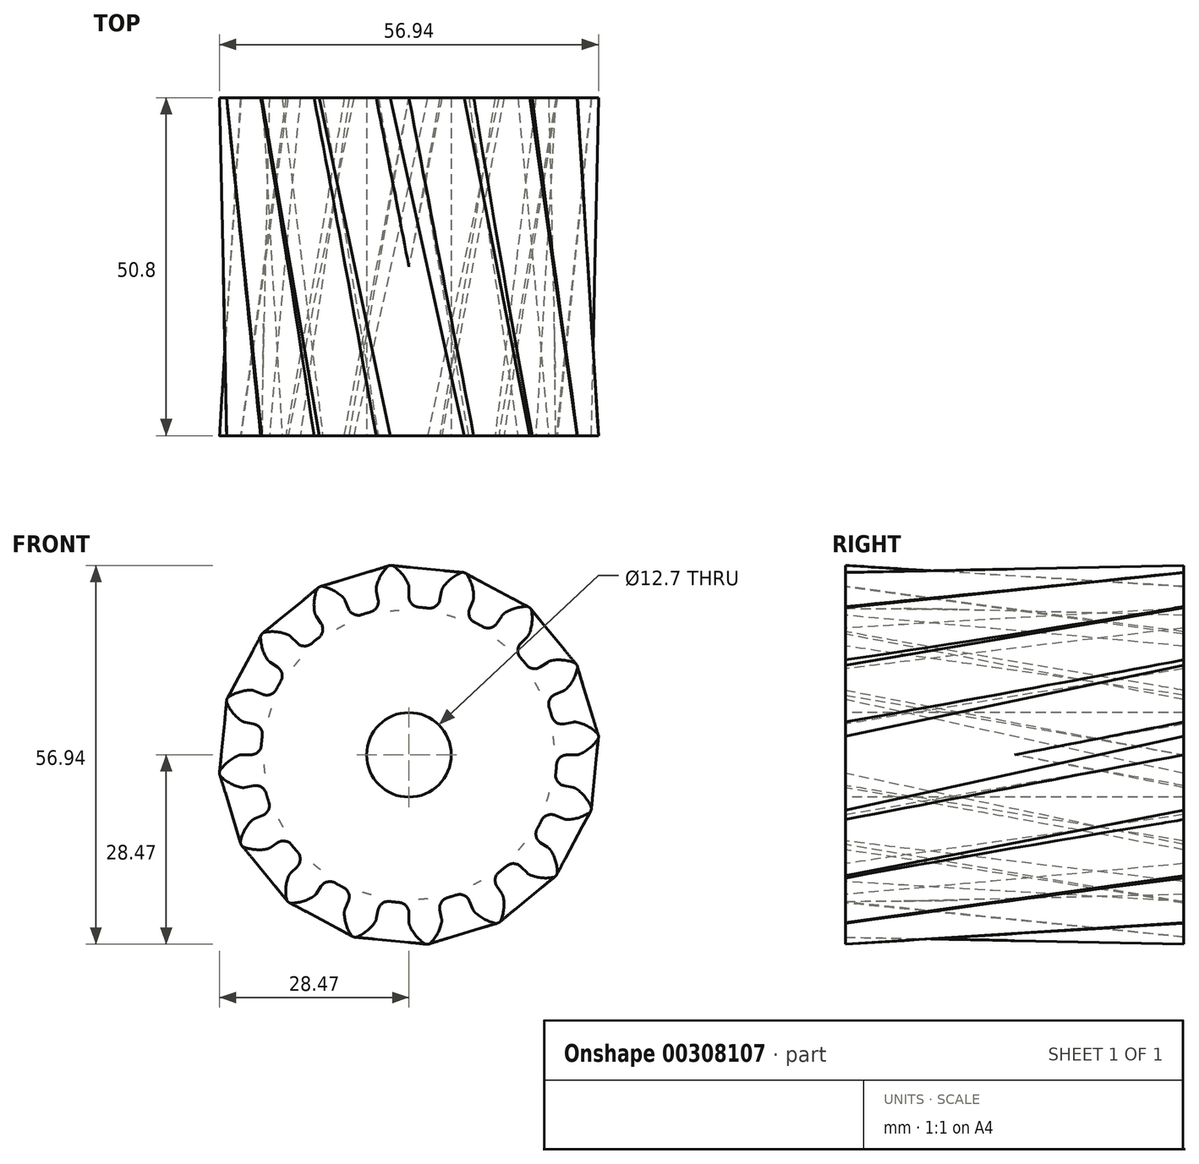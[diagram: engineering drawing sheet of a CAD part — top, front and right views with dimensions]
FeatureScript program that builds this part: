
annotation { "Feature Type Name" : "Feature", "Feature Type Description" : "" }
export const myFeature = defineFeature(function(context is Context, id is Id, definition is map)
    precondition{}
    {
        {
            var Q0;
            Q0=qCreatedBy(makeId("Front.planeOp"),FACE);
            var sketch = newSketch(context, id + "F0", { "sketchPlane" : qUnion([Q0])});
            skArc(sketch, "E0", {"start": v(-5.78, 21.46) * mm, "mid": v(-6.45, 21.27) * mm, "end": v(-7.11, 21.06) * mm});
            skArc(sketch, "E1.trimOffspring", {"start": v(-0.14, 25.74) * mm, "mid": v(-1.06, 27.21) * mm, "end": v(-2.36, 28.38) * mm});
            skLineSegment(sketch, "E2", {"start": v(-2.64, 28.47) * mm, "end": v(-2.8, 28.47) * mm});
            skLineSegment(sketch, "E3", {"start": v(0, 25.08) * mm, "end": v(0, 23.76) * mm});
            skLineSegment(sketch, "E4.MirrorCS", {"start": v(-2.96, 28.44) * mm, "end": v(-2.8, 28.47) * mm});
            skArc(sketch, "E5.MirrorCS", {"start": v(-4.89, 25.27) * mm, "mid": v(-4.27, 26.9) * mm, "end": v(-3.22, 28.3) * mm});
            skLineSegment(sketch, "E6.MirrorCS", {"start": v(-4.9, 24.6) * mm, "end": v(-4.64, 23.3) * mm});
            skPoint(sketch, "E7.orphan", {"position": v(-4.19, 21.03) * mm});
            skPoint(sketch, "E8.orphan", {"position": v(0, 21.44) * mm});
            skPoint(sketch, "E9.visualSharp", {"position": v(-3.1, 28.4) * mm});
            skArc(sketch, "E9.filletArc", {"start": v(-2.96, 28.44) * mm, "mid": v(-3.1, 28.38) * mm, "end": v(-3.22, 28.3) * mm});
            skPoint(sketch, "E10.visualSharp", {"position": v(-2.5, 28.47) * mm});
            skArc(sketch, "E10.filletArc", {"start": v(-2.36, 28.38) * mm, "mid": v(-2.5, 28.44) * mm, "end": v(-2.64, 28.47) * mm});
            skPoint(sketch, "E11.visualSharp", {"position": v(-4.96, 24.91) * mm});
            skArc(sketch, "E11.filletArc", {"start": v(-4.89, 25.27) * mm, "mid": v(-4.93, 24.94) * mm, "end": v(-4.9, 24.6) * mm});
            skPoint(sketch, "E12.visualSharp", {"position": v(0, 25.4) * mm});
            skArc(sketch, "E12.filletArc", {"start": v(0, 25.08) * mm, "mid": v(-0.03, 25.42) * mm, "end": v(-0.14, 25.74) * mm});
            skPoint(sketch, "E13.visualSharp", {"position": v(-4.34, 21.8) * mm});
            skArc(sketch, "E13.filletArc", {"start": v(-5.78, 21.46) * mm, "mid": v(-4.85, 22.15) * mm, "end": v(-4.64, 23.3) * mm});
            skPoint(sketch, "E14.visualSharp", {"position": v(0, 22.22) * mm});
            skArc(sketch, "E14.filletArc", {"start": v(0, 23.76) * mm, "mid": v(0.43, 22.67) * mm, "end": v(1.49, 22.18) * mm});
            skArc(sketch, "E15.1.0", {"start": v(-13.56, 17.61) * mm, "mid": v(-12.96, 18.61) * mm, "end": v(-13.2, 19.75) * mm});
            skLineSegment(sketch, "E15.1.1", {"start": v(-13.94, 20.85) * mm, "end": v(-13.2, 19.75) * mm});
            skArc(sketch, "E15.1.2", {"start": v(-14.19, 21.47) * mm, "mid": v(-14.1, 21.15) * mm, "end": v(-13.94, 20.85) * mm});
            skArc(sketch, "E15.1.3", {"start": v(-14.19, 21.47) * mm, "mid": v(-14.23, 23.22) * mm, "end": v(-13.8, 24.9) * mm});
            skArc(sketch, "E15.1.4", {"start": v(-13.62, 25.14) * mm, "mid": v(-13.73, 25.04) * mm, "end": v(-13.8, 24.9) * mm});
            skLineSegment(sketch, "E15.1.5", {"start": v(-13.62, 25.14) * mm, "end": v(-13.48, 25.23) * mm});
            skLineSegment(sketch, "E15.1.6", {"start": v(-13.34, 25.29) * mm, "end": v(-13.48, 25.23) * mm});
            skArc(sketch, "E15.1.7", {"start": v(-13.04, 25.32) * mm, "mid": v(-13.2, 25.32) * mm, "end": v(-13.34, 25.29) * mm});
            skArc(sketch, "E15.1.8", {"start": v(-9.97, 23.73) * mm, "mid": v(-11.4, 24.73) * mm, "end": v(-13.04, 25.32) * mm});
            skArc(sketch, "E15.1.9", {"start": v(-9.6, 23.18) * mm, "mid": v(-9.75, 23.47) * mm, "end": v(-9.97, 23.73) * mm});
            skLineSegment(sketch, "E15.1.10", {"start": v(-9.6, 23.18) * mm, "end": v(-9.09, 21.95) * mm});
            skArc(sketch, "E15.1.11", {"start": v(-9.09, 21.95) * mm, "mid": v(-8.28, 21.11) * mm, "end": v(-7.11, 21.06) * mm});
            skArc(sketch, "E15.2.0", {"start": v(-19.26, 11.08) * mm, "mid": v(-19.1, 12.24) * mm, "end": v(-19.76, 13.2) * mm});
            skLineSegment(sketch, "E15.2.1", {"start": v(-20.86, 13.93) * mm, "end": v(-19.76, 13.2) * mm});
            skArc(sketch, "E15.2.2", {"start": v(-21.32, 14.41) * mm, "mid": v(-21.12, 14.15) * mm, "end": v(-20.86, 13.93) * mm});
            skArc(sketch, "E15.2.3", {"start": v(-21.32, 14.41) * mm, "mid": v(-22.03, 16) * mm, "end": v(-22.29, 17.73) * mm});
            skArc(sketch, "E15.2.4", {"start": v(-22.2, 18.01) * mm, "mid": v(-22.26, 17.88) * mm, "end": v(-22.29, 17.73) * mm});
            skLineSegment(sketch, "E15.2.5", {"start": v(-22.2, 18.01) * mm, "end": v(-22.11, 18.15) * mm});
            skLineSegment(sketch, "E15.2.6", {"start": v(-22, 18.26) * mm, "end": v(-22.11, 18.15) * mm});
            skArc(sketch, "E15.2.7", {"start": v(-21.74, 18.4) * mm, "mid": v(-21.88, 18.35) * mm, "end": v(-22, 18.26) * mm});
            skArc(sketch, "E15.2.8", {"start": v(-18.3, 18.1) * mm, "mid": v(-20, 18.49) * mm, "end": v(-21.74, 18.4) * mm});
            skArc(sketch, "E15.2.9", {"start": v(-17.73, 17.74) * mm, "mid": v(-18, 17.95) * mm, "end": v(-18.3, 18.1) * mm});
            skLineSegment(sketch, "E15.2.10", {"start": v(-17.73, 17.74) * mm, "end": v(-16.8, 16.8) * mm});
            skArc(sketch, "E15.2.11", {"start": v(-16.8, 16.8) * mm, "mid": v(-15.73, 16.34) * mm, "end": v(-14.63, 16.73) * mm});
            skArc(sketch, "E15.3.0", {"start": v(-22.04, 2.87) * mm, "mid": v(-22.32, 4) * mm, "end": v(-23.3, 4.63) * mm});
            skLineSegment(sketch, "E15.3.1", {"start": v(-24.6, 4.89) * mm, "end": v(-23.3, 4.63) * mm});
            skArc(sketch, "E15.3.2", {"start": v(-25.22, 5.15) * mm, "mid": v(-24.92, 4.99) * mm, "end": v(-24.6, 4.89) * mm});
            skArc(sketch, "E15.3.3", {"start": v(-25.22, 5.15) * mm, "mid": v(-26.48, 6.35) * mm, "end": v(-27.37, 7.85) * mm});
            skArc(sketch, "E15.3.4", {"start": v(-27.4, 8.15) * mm, "mid": v(-27.41, 8) * mm, "end": v(-27.37, 7.85) * mm});
            skLineSegment(sketch, "E15.3.5", {"start": v(-27.4, 8.15) * mm, "end": v(-27.37, 8.3) * mm});
            skLineSegment(sketch, "E15.3.6", {"start": v(-27.31, 8.45) * mm, "end": v(-27.37, 8.3) * mm});
            skArc(sketch, "E15.3.7", {"start": v(-27.12, 8.68) * mm, "mid": v(-27.23, 8.58) * mm, "end": v(-27.31, 8.45) * mm});
            skArc(sketch, "E15.3.8", {"start": v(-23.83, 9.72) * mm, "mid": v(-25.55, 9.43) * mm, "end": v(-27.12, 8.68) * mm});
            skArc(sketch, "E15.3.9", {"start": v(-23.17, 9.6) * mm, "mid": v(-23.5, 9.7) * mm, "end": v(-23.83, 9.72) * mm});
            skLineSegment(sketch, "E15.3.10", {"start": v(-23.17, 9.6) * mm, "end": v(-21.95, 9.1) * mm});
            skArc(sketch, "E15.3.11", {"start": v(-21.95, 9.1) * mm, "mid": v(-20.78, 9.08) * mm, "end": v(-19.92, 9.86) * mm});
            skArc(sketch, "E15.4.0", {"start": v(-21.46, -5.78) * mm, "mid": v(-22.15, -4.85) * mm, "end": v(-23.3, -4.64) * mm});
            skLineSegment(sketch, "E15.4.1", {"start": v(-24.6, -4.9) * mm, "end": v(-23.3, -4.64) * mm});
            skArc(sketch, "E15.4.2", {"start": v(-25.27, -4.89) * mm, "mid": v(-24.94, -4.93) * mm, "end": v(-24.6, -4.9) * mm});
            skArc(sketch, "E15.4.3", {"start": v(-25.27, -4.89) * mm, "mid": v(-26.9, -4.27) * mm, "end": v(-28.3, -3.22) * mm});
            skArc(sketch, "E15.4.4", {"start": v(-28.44, -2.96) * mm, "mid": v(-28.38, -3.1) * mm, "end": v(-28.3, -3.22) * mm});
            skLineSegment(sketch, "E15.4.5", {"start": v(-28.44, -2.96) * mm, "end": v(-28.47, -2.8) * mm});
            skLineSegment(sketch, "E15.4.6", {"start": v(-28.47, -2.64) * mm, "end": v(-28.47, -2.8) * mm});
            skArc(sketch, "E15.4.7", {"start": v(-28.38, -2.36) * mm, "mid": v(-28.44, -2.5) * mm, "end": v(-28.47, -2.64) * mm});
            skArc(sketch, "E15.4.8", {"start": v(-25.74, -0.14) * mm, "mid": v(-27.21, -1.06) * mm, "end": v(-28.38, -2.36) * mm});
            skArc(sketch, "E15.4.9", {"start": v(-25.08, 0) * mm, "mid": v(-25.42, -0.03) * mm, "end": v(-25.74, -0.14) * mm});
            skLineSegment(sketch, "E15.4.10", {"start": v(-25.08, 0) * mm, "end": v(-23.76, 0) * mm});
            skArc(sketch, "E15.4.11", {"start": v(-23.76, 0) * mm, "mid": v(-22.67, 0.43) * mm, "end": v(-22.18, 1.49) * mm});
            skArc(sketch, "E15.5.0", {"start": v(-17.61, -13.56) * mm, "mid": v(-18.61, -12.96) * mm, "end": v(-19.75, -13.2) * mm});
            skLineSegment(sketch, "E15.5.1", {"start": v(-20.85, -13.94) * mm, "end": v(-19.75, -13.2) * mm});
            skArc(sketch, "E15.5.2", {"start": v(-21.47, -14.19) * mm, "mid": v(-21.15, -14.1) * mm, "end": v(-20.85, -13.94) * mm});
            skArc(sketch, "E15.5.3", {"start": v(-21.47, -14.19) * mm, "mid": v(-23.22, -14.23) * mm, "end": v(-24.9, -13.8) * mm});
            skArc(sketch, "E15.5.4", {"start": v(-25.14, -13.62) * mm, "mid": v(-25.04, -13.73) * mm, "end": v(-24.9, -13.8) * mm});
            skLineSegment(sketch, "E15.5.5", {"start": v(-25.14, -13.62) * mm, "end": v(-25.23, -13.48) * mm});
            skLineSegment(sketch, "E15.5.6", {"start": v(-25.29, -13.34) * mm, "end": v(-25.23, -13.48) * mm});
            skArc(sketch, "E15.5.7", {"start": v(-25.32, -13.04) * mm, "mid": v(-25.32, -13.2) * mm, "end": v(-25.29, -13.34) * mm});
            skArc(sketch, "E15.5.8", {"start": v(-23.73, -9.97) * mm, "mid": v(-24.73, -11.4) * mm, "end": v(-25.32, -13.04) * mm});
            skArc(sketch, "E15.5.9", {"start": v(-23.18, -9.6) * mm, "mid": v(-23.47, -9.75) * mm, "end": v(-23.73, -9.97) * mm});
            skLineSegment(sketch, "E15.5.10", {"start": v(-23.18, -9.6) * mm, "end": v(-21.95, -9.09) * mm});
            skArc(sketch, "E15.5.11", {"start": v(-21.95, -9.09) * mm, "mid": v(-21.11, -8.28) * mm, "end": v(-21.06, -7.11) * mm});
            skArc(sketch, "E15.6.0", {"start": v(-11.08, -19.26) * mm, "mid": v(-12.24, -19.1) * mm, "end": v(-13.2, -19.76) * mm});
            skLineSegment(sketch, "E15.6.1", {"start": v(-13.93, -20.86) * mm, "end": v(-13.2, -19.76) * mm});
            skArc(sketch, "E15.6.2", {"start": v(-14.41, -21.32) * mm, "mid": v(-14.15, -21.12) * mm, "end": v(-13.93, -20.86) * mm});
            skArc(sketch, "E15.6.3", {"start": v(-14.41, -21.32) * mm, "mid": v(-16, -22.03) * mm, "end": v(-17.73, -22.29) * mm});
            skArc(sketch, "E15.6.4", {"start": v(-18.01, -22.2) * mm, "mid": v(-17.88, -22.26) * mm, "end": v(-17.73, -22.29) * mm});
            skLineSegment(sketch, "E15.6.5", {"start": v(-18.01, -22.2) * mm, "end": v(-18.15, -22.11) * mm});
            skLineSegment(sketch, "E15.6.6", {"start": v(-18.26, -22) * mm, "end": v(-18.15, -22.11) * mm});
            skArc(sketch, "E15.6.7", {"start": v(-18.4, -21.74) * mm, "mid": v(-18.35, -21.88) * mm, "end": v(-18.26, -22) * mm});
            skArc(sketch, "E15.6.8", {"start": v(-18.1, -18.3) * mm, "mid": v(-18.49, -20) * mm, "end": v(-18.4, -21.74) * mm});
            skArc(sketch, "E15.6.9", {"start": v(-17.74, -17.73) * mm, "mid": v(-17.95, -18) * mm, "end": v(-18.1, -18.3) * mm});
            skLineSegment(sketch, "E15.6.10", {"start": v(-17.74, -17.73) * mm, "end": v(-16.8, -16.8) * mm});
            skArc(sketch, "E15.6.11", {"start": v(-16.8, -16.8) * mm, "mid": v(-16.34, -15.73) * mm, "end": v(-16.73, -14.63) * mm});
            skArc(sketch, "E15.7.0", {"start": v(-2.87, -22.04) * mm, "mid": v(-4, -22.32) * mm, "end": v(-4.63, -23.3) * mm});
            skLineSegment(sketch, "E15.7.1", {"start": v(-4.89, -24.6) * mm, "end": v(-4.63, -23.3) * mm});
            skArc(sketch, "E15.7.2", {"start": v(-5.15, -25.22) * mm, "mid": v(-4.99, -24.92) * mm, "end": v(-4.89, -24.6) * mm});
            skArc(sketch, "E15.7.3", {"start": v(-5.15, -25.22) * mm, "mid": v(-6.35, -26.48) * mm, "end": v(-7.85, -27.37) * mm});
            skArc(sketch, "E15.7.4", {"start": v(-8.15, -27.4) * mm, "mid": v(-8, -27.41) * mm, "end": v(-7.85, -27.37) * mm});
            skLineSegment(sketch, "E15.7.5", {"start": v(-8.15, -27.4) * mm, "end": v(-8.3, -27.37) * mm});
            skLineSegment(sketch, "E15.7.6", {"start": v(-8.45, -27.31) * mm, "end": v(-8.3, -27.37) * mm});
            skArc(sketch, "E15.7.7", {"start": v(-8.68, -27.12) * mm, "mid": v(-8.58, -27.23) * mm, "end": v(-8.45, -27.31) * mm});
            skArc(sketch, "E15.7.8", {"start": v(-9.72, -23.83) * mm, "mid": v(-9.43, -25.55) * mm, "end": v(-8.68, -27.12) * mm});
            skArc(sketch, "E15.7.9", {"start": v(-9.6, -23.17) * mm, "mid": v(-9.7, -23.5) * mm, "end": v(-9.72, -23.83) * mm});
            skLineSegment(sketch, "E15.7.10", {"start": v(-9.6, -23.17) * mm, "end": v(-9.1, -21.95) * mm});
            skArc(sketch, "E15.7.11", {"start": v(-9.1, -21.95) * mm, "mid": v(-9.08, -20.78) * mm, "end": v(-9.86, -19.92) * mm});
            skArc(sketch, "E15.8.0", {"start": v(5.78, -21.46) * mm, "mid": v(4.85, -22.15) * mm, "end": v(4.64, -23.3) * mm});
            skLineSegment(sketch, "E15.8.1", {"start": v(4.9, -24.6) * mm, "end": v(4.64, -23.3) * mm});
            skArc(sketch, "E15.8.2", {"start": v(4.89, -25.27) * mm, "mid": v(4.93, -24.94) * mm, "end": v(4.9, -24.6) * mm});
            skArc(sketch, "E15.8.3", {"start": v(4.89, -25.27) * mm, "mid": v(4.27, -26.9) * mm, "end": v(3.22, -28.3) * mm});
            skArc(sketch, "E15.8.4", {"start": v(2.96, -28.44) * mm, "mid": v(3.1, -28.38) * mm, "end": v(3.22, -28.3) * mm});
            skLineSegment(sketch, "E15.8.5", {"start": v(2.96, -28.44) * mm, "end": v(2.8, -28.47) * mm});
            skLineSegment(sketch, "E15.8.6", {"start": v(2.64, -28.47) * mm, "end": v(2.8, -28.47) * mm});
            skArc(sketch, "E15.8.7", {"start": v(2.36, -28.38) * mm, "mid": v(2.5, -28.44) * mm, "end": v(2.64, -28.47) * mm});
            skArc(sketch, "E15.8.8", {"start": v(0.14, -25.74) * mm, "mid": v(1.06, -27.21) * mm, "end": v(2.36, -28.38) * mm});
            skArc(sketch, "E15.8.9", {"start": v(0, -25.08) * mm, "mid": v(0.03, -25.42) * mm, "end": v(0.14, -25.74) * mm});
            skLineSegment(sketch, "E15.8.10", {"start": v(0, -25.08) * mm, "end": v(0, -23.76) * mm});
            skArc(sketch, "E15.8.11", {"start": v(0, -23.76) * mm, "mid": v(-0.43, -22.67) * mm, "end": v(-1.49, -22.18) * mm});
            skArc(sketch, "E15.9.0", {"start": v(13.56, -17.61) * mm, "mid": v(12.96, -18.61) * mm, "end": v(13.2, -19.75) * mm});
            skLineSegment(sketch, "E15.9.1", {"start": v(13.94, -20.85) * mm, "end": v(13.2, -19.75) * mm});
            skArc(sketch, "E15.9.2", {"start": v(14.19, -21.47) * mm, "mid": v(14.1, -21.15) * mm, "end": v(13.94, -20.85) * mm});
            skArc(sketch, "E15.9.3", {"start": v(14.19, -21.47) * mm, "mid": v(14.23, -23.22) * mm, "end": v(13.8, -24.9) * mm});
            skArc(sketch, "E15.9.4", {"start": v(13.62, -25.14) * mm, "mid": v(13.73, -25.04) * mm, "end": v(13.8, -24.9) * mm});
            skLineSegment(sketch, "E15.9.5", {"start": v(13.62, -25.14) * mm, "end": v(13.48, -25.23) * mm});
            skLineSegment(sketch, "E15.9.6", {"start": v(13.34, -25.29) * mm, "end": v(13.48, -25.23) * mm});
            skArc(sketch, "E15.9.7", {"start": v(13.04, -25.32) * mm, "mid": v(13.2, -25.32) * mm, "end": v(13.34, -25.29) * mm});
            skArc(sketch, "E15.9.8", {"start": v(9.97, -23.73) * mm, "mid": v(11.4, -24.73) * mm, "end": v(13.04, -25.32) * mm});
            skArc(sketch, "E15.9.9", {"start": v(9.6, -23.18) * mm, "mid": v(9.75, -23.47) * mm, "end": v(9.97, -23.73) * mm});
            skLineSegment(sketch, "E15.9.10", {"start": v(9.6, -23.18) * mm, "end": v(9.09, -21.95) * mm});
            skArc(sketch, "E15.9.11", {"start": v(9.09, -21.95) * mm, "mid": v(8.28, -21.11) * mm, "end": v(7.11, -21.06) * mm});
            skArc(sketch, "E15.10.0", {"start": v(19.26, -11.08) * mm, "mid": v(19.1, -12.24) * mm, "end": v(19.76, -13.2) * mm});
            skLineSegment(sketch, "E15.10.1", {"start": v(20.86, -13.93) * mm, "end": v(19.76, -13.2) * mm});
            skArc(sketch, "E15.10.2", {"start": v(21.32, -14.41) * mm, "mid": v(21.12, -14.15) * mm, "end": v(20.86, -13.93) * mm});
            skArc(sketch, "E15.10.3", {"start": v(21.32, -14.41) * mm, "mid": v(22.03, -16) * mm, "end": v(22.29, -17.73) * mm});
            skArc(sketch, "E15.10.4", {"start": v(22.2, -18.01) * mm, "mid": v(22.26, -17.88) * mm, "end": v(22.29, -17.73) * mm});
            skLineSegment(sketch, "E15.10.5", {"start": v(22.2, -18.01) * mm, "end": v(22.11, -18.15) * mm});
            skLineSegment(sketch, "E15.10.6", {"start": v(22, -18.26) * mm, "end": v(22.11, -18.15) * mm});
            skArc(sketch, "E15.10.7", {"start": v(21.74, -18.4) * mm, "mid": v(21.88, -18.35) * mm, "end": v(22, -18.26) * mm});
            skArc(sketch, "E15.10.8", {"start": v(18.3, -18.1) * mm, "mid": v(20, -18.49) * mm, "end": v(21.74, -18.4) * mm});
            skArc(sketch, "E15.10.9", {"start": v(17.73, -17.74) * mm, "mid": v(18, -17.95) * mm, "end": v(18.3, -18.1) * mm});
            skLineSegment(sketch, "E15.10.10", {"start": v(17.73, -17.74) * mm, "end": v(16.8, -16.8) * mm});
            skArc(sketch, "E15.10.11", {"start": v(16.8, -16.8) * mm, "mid": v(15.73, -16.34) * mm, "end": v(14.63, -16.73) * mm});
            skArc(sketch, "E15.11.0", {"start": v(22.04, -2.87) * mm, "mid": v(22.32, -4) * mm, "end": v(23.3, -4.63) * mm});
            skLineSegment(sketch, "E15.11.1", {"start": v(24.6, -4.89) * mm, "end": v(23.3, -4.63) * mm});
            skArc(sketch, "E15.11.2", {"start": v(25.22, -5.15) * mm, "mid": v(24.92, -4.99) * mm, "end": v(24.6, -4.89) * mm});
            skArc(sketch, "E15.11.3", {"start": v(25.22, -5.15) * mm, "mid": v(26.48, -6.35) * mm, "end": v(27.37, -7.85) * mm});
            skArc(sketch, "E15.11.4", {"start": v(27.4, -8.15) * mm, "mid": v(27.41, -8) * mm, "end": v(27.37, -7.85) * mm});
            skLineSegment(sketch, "E15.11.5", {"start": v(27.4, -8.15) * mm, "end": v(27.37, -8.3) * mm});
            skLineSegment(sketch, "E15.11.6", {"start": v(27.31, -8.45) * mm, "end": v(27.37, -8.3) * mm});
            skArc(sketch, "E15.11.7", {"start": v(27.12, -8.68) * mm, "mid": v(27.23, -8.58) * mm, "end": v(27.31, -8.45) * mm});
            skArc(sketch, "E15.11.8", {"start": v(23.83, -9.72) * mm, "mid": v(25.55, -9.43) * mm, "end": v(27.12, -8.68) * mm});
            skArc(sketch, "E15.11.9", {"start": v(23.17, -9.6) * mm, "mid": v(23.5, -9.7) * mm, "end": v(23.83, -9.72) * mm});
            skLineSegment(sketch, "E15.11.10", {"start": v(23.17, -9.6) * mm, "end": v(21.95, -9.1) * mm});
            skArc(sketch, "E15.11.11", {"start": v(21.95, -9.1) * mm, "mid": v(20.78, -9.08) * mm, "end": v(19.92, -9.86) * mm});
            skArc(sketch, "E15.12.0", {"start": v(21.46, 5.78) * mm, "mid": v(22.15, 4.85) * mm, "end": v(23.3, 4.64) * mm});
            skLineSegment(sketch, "E15.12.1", {"start": v(24.6, 4.9) * mm, "end": v(23.3, 4.64) * mm});
            skArc(sketch, "E15.12.2", {"start": v(25.27, 4.89) * mm, "mid": v(24.94, 4.93) * mm, "end": v(24.6, 4.9) * mm});
            skArc(sketch, "E15.12.3", {"start": v(25.27, 4.89) * mm, "mid": v(26.9, 4.27) * mm, "end": v(28.3, 3.22) * mm});
            skArc(sketch, "E15.12.4", {"start": v(28.44, 2.96) * mm, "mid": v(28.38, 3.1) * mm, "end": v(28.3, 3.22) * mm});
            skLineSegment(sketch, "E15.12.5", {"start": v(28.44, 2.96) * mm, "end": v(28.47, 2.8) * mm});
            skLineSegment(sketch, "E15.12.6", {"start": v(28.47, 2.64) * mm, "end": v(28.47, 2.8) * mm});
            skArc(sketch, "E15.12.7", {"start": v(28.38, 2.36) * mm, "mid": v(28.44, 2.5) * mm, "end": v(28.47, 2.64) * mm});
            skArc(sketch, "E15.12.8", {"start": v(25.74, 0.14) * mm, "mid": v(27.21, 1.06) * mm, "end": v(28.38, 2.36) * mm});
            skArc(sketch, "E15.12.9", {"start": v(25.08, 0) * mm, "mid": v(25.42, 0.03) * mm, "end": v(25.74, 0.14) * mm});
            skLineSegment(sketch, "E15.12.10", {"start": v(25.08, 0) * mm, "end": v(23.76, 0) * mm});
            skArc(sketch, "E15.12.11", {"start": v(23.76, 0) * mm, "mid": v(22.67, -0.43) * mm, "end": v(22.18, -1.49) * mm});
            skArc(sketch, "E15.13.0", {"start": v(17.61, 13.56) * mm, "mid": v(18.61, 12.96) * mm, "end": v(19.75, 13.2) * mm});
            skLineSegment(sketch, "E15.13.1", {"start": v(20.85, 13.94) * mm, "end": v(19.75, 13.2) * mm});
            skArc(sketch, "E15.13.2", {"start": v(21.47, 14.19) * mm, "mid": v(21.15, 14.1) * mm, "end": v(20.85, 13.94) * mm});
            skArc(sketch, "E15.13.3", {"start": v(21.47, 14.19) * mm, "mid": v(23.22, 14.23) * mm, "end": v(24.9, 13.8) * mm});
            skArc(sketch, "E15.13.4", {"start": v(25.14, 13.62) * mm, "mid": v(25.04, 13.73) * mm, "end": v(24.9, 13.8) * mm});
            skLineSegment(sketch, "E15.13.5", {"start": v(25.14, 13.62) * mm, "end": v(25.23, 13.48) * mm});
            skLineSegment(sketch, "E15.13.6", {"start": v(25.29, 13.34) * mm, "end": v(25.23, 13.48) * mm});
            skArc(sketch, "E15.13.7", {"start": v(25.32, 13.04) * mm, "mid": v(25.32, 13.2) * mm, "end": v(25.29, 13.34) * mm});
            skArc(sketch, "E15.13.8", {"start": v(23.73, 9.97) * mm, "mid": v(24.73, 11.4) * mm, "end": v(25.32, 13.04) * mm});
            skArc(sketch, "E15.13.9", {"start": v(23.18, 9.6) * mm, "mid": v(23.47, 9.75) * mm, "end": v(23.73, 9.97) * mm});
            skLineSegment(sketch, "E15.13.10", {"start": v(23.18, 9.6) * mm, "end": v(21.95, 9.09) * mm});
            skArc(sketch, "E15.13.11", {"start": v(21.95, 9.09) * mm, "mid": v(21.11, 8.28) * mm, "end": v(21.06, 7.11) * mm});
            skArc(sketch, "E15.14.0", {"start": v(11.08, 19.26) * mm, "mid": v(12.24, 19.1) * mm, "end": v(13.2, 19.76) * mm});
            skLineSegment(sketch, "E15.14.1", {"start": v(13.93, 20.86) * mm, "end": v(13.2, 19.76) * mm});
            skArc(sketch, "E15.14.2", {"start": v(14.41, 21.32) * mm, "mid": v(14.15, 21.12) * mm, "end": v(13.93, 20.86) * mm});
            skArc(sketch, "E15.14.3", {"start": v(14.41, 21.32) * mm, "mid": v(16, 22.03) * mm, "end": v(17.73, 22.29) * mm});
            skArc(sketch, "E15.14.4", {"start": v(18.01, 22.2) * mm, "mid": v(17.88, 22.26) * mm, "end": v(17.73, 22.29) * mm});
            skLineSegment(sketch, "E15.14.5", {"start": v(18.01, 22.2) * mm, "end": v(18.15, 22.11) * mm});
            skLineSegment(sketch, "E15.14.6", {"start": v(18.26, 22) * mm, "end": v(18.15, 22.11) * mm});
            skArc(sketch, "E15.14.7", {"start": v(18.4, 21.74) * mm, "mid": v(18.35, 21.88) * mm, "end": v(18.26, 22) * mm});
            skArc(sketch, "E15.14.8", {"start": v(18.1, 18.3) * mm, "mid": v(18.49, 20) * mm, "end": v(18.4, 21.74) * mm});
            skArc(sketch, "E15.14.9", {"start": v(17.74, 17.73) * mm, "mid": v(17.95, 18) * mm, "end": v(18.1, 18.3) * mm});
            skLineSegment(sketch, "E15.14.10", {"start": v(17.74, 17.73) * mm, "end": v(16.8, 16.8) * mm});
            skArc(sketch, "E15.14.11", {"start": v(16.8, 16.8) * mm, "mid": v(16.34, 15.73) * mm, "end": v(16.73, 14.63) * mm});
            skArc(sketch, "E15.15.0", {"start": v(2.87, 22.04) * mm, "mid": v(4, 22.32) * mm, "end": v(4.63, 23.3) * mm});
            skLineSegment(sketch, "E15.15.1", {"start": v(4.89, 24.6) * mm, "end": v(4.63, 23.3) * mm});
            skArc(sketch, "E15.15.2", {"start": v(5.15, 25.22) * mm, "mid": v(4.99, 24.92) * mm, "end": v(4.89, 24.6) * mm});
            skArc(sketch, "E15.15.3", {"start": v(5.15, 25.22) * mm, "mid": v(6.35, 26.48) * mm, "end": v(7.85, 27.37) * mm});
            skArc(sketch, "E15.15.4", {"start": v(8.15, 27.4) * mm, "mid": v(8, 27.41) * mm, "end": v(7.85, 27.37) * mm});
            skLineSegment(sketch, "E15.15.5", {"start": v(8.15, 27.4) * mm, "end": v(8.3, 27.37) * mm});
            skLineSegment(sketch, "E15.15.6", {"start": v(8.45, 27.31) * mm, "end": v(8.3, 27.37) * mm});
            skArc(sketch, "E15.15.7", {"start": v(8.68, 27.12) * mm, "mid": v(8.58, 27.23) * mm, "end": v(8.45, 27.31) * mm});
            skArc(sketch, "E15.15.8", {"start": v(9.72, 23.83) * mm, "mid": v(9.43, 25.55) * mm, "end": v(8.68, 27.12) * mm});
            skArc(sketch, "E15.15.9", {"start": v(9.6, 23.17) * mm, "mid": v(9.7, 23.5) * mm, "end": v(9.72, 23.83) * mm});
            skLineSegment(sketch, "E15.15.10", {"start": v(9.6, 23.17) * mm, "end": v(9.1, 21.95) * mm});
            skArc(sketch, "E15.15.11", {"start": v(9.1, 21.95) * mm, "mid": v(9.08, 20.78) * mm, "end": v(9.86, 19.92) * mm});
            skArc(sketch, "E16.trimOffspring", {"start": v(-17.61, -13.56) * mm, "mid": v(-17.18, -14.1) * mm, "end": v(-16.73, -14.63) * mm});
            skArc(sketch, "E17.trimOffspring", {"start": v(-21.46, -5.78) * mm, "mid": v(-21.27, -6.45) * mm, "end": v(-21.06, -7.11) * mm});
            skArc(sketch, "E18.trimOffspring", {"start": v(-22.04, 2.87) * mm, "mid": v(-22.12, 2.18) * mm, "end": v(-22.18, 1.49) * mm});
            skArc(sketch, "E19.trimOffspring", {"start": v(-19.26, 11.08) * mm, "mid": v(-19.6, 10.48) * mm, "end": v(-19.92, 9.86) * mm});
            skArc(sketch, "E20.trimOffspring", {"start": v(-13.56, 17.61) * mm, "mid": v(-14.1, 17.18) * mm, "end": v(-14.63, 16.73) * mm});
            skArc(sketch, "E21.trimOffspring", {"start": v(2.87, 22.04) * mm, "mid": v(2.18, 22.12) * mm, "end": v(1.49, 22.18) * mm});
            skArc(sketch, "E22.trimOffspring", {"start": v(11.08, 19.26) * mm, "mid": v(10.48, 19.6) * mm, "end": v(9.86, 19.92) * mm});
            skArc(sketch, "E23.trimOffspring", {"start": v(17.61, 13.56) * mm, "mid": v(17.18, 14.1) * mm, "end": v(16.73, 14.63) * mm});
            skArc(sketch, "E24.trimOffspring", {"start": v(21.46, 5.78) * mm, "mid": v(21.27, 6.45) * mm, "end": v(21.06, 7.11) * mm});
            skArc(sketch, "E25.trimOffspring", {"start": v(22.04, -2.87) * mm, "mid": v(22.12, -2.18) * mm, "end": v(22.18, -1.49) * mm});
            skArc(sketch, "E26.trimOffspring", {"start": v(-2.87, -22.04) * mm, "mid": v(-2.18, -22.12) * mm, "end": v(-1.49, -22.18) * mm});
            skArc(sketch, "E27.trimOffspring", {"start": v(-11.08, -19.26) * mm, "mid": v(-10.48, -19.6) * mm, "end": v(-9.86, -19.92) * mm});
            skArc(sketch, "E28.trimOffspring", {"start": v(5.78, -21.46) * mm, "mid": v(6.45, -21.27) * mm, "end": v(7.11, -21.06) * mm});
            skArc(sketch, "E29.trimOffspring", {"start": v(13.56, -17.61) * mm, "mid": v(14.1, -17.18) * mm, "end": v(14.63, -16.73) * mm});
            skArc(sketch, "E30.trimOffspring", {"start": v(19.26, -11.08) * mm, "mid": v(19.6, -10.48) * mm, "end": v(19.92, -9.86) * mm});
            skSolve(sketch);
        }
        {
            var Q0;
            Q0=makeQuery(id+"F0.imprint","IMPRINT",FACE,{"disambiguationData":[TD([[makeQuery(id+"F0.imprint","IMPRINT",EDGE,{"derivedFrom":sQuery(id+"F0.wireOp",EDGE,"E0")}),1.0]])]});
            cPlane(context, id + "F1", {"entities" : qUnion([Q0]), "cplaneType" : CPlaneType.OFFSET, "offset" : 50.8 * mm, "width" : 152.4 * mm, "height" : 152.4 * mm});
        }
        {
            var Q0;
            Q0=qCreatedBy(id+"F1.planeOp",FACE);
            var sketch = newSketch(context, id + "F2", { "sketchPlane" : qUnion([Q0])});
            skArc(sketch, "E31.0.0", {"start": v(-22.29, 17.73) * mm, "mid": v(-22.03, 16) * mm, "end": v(-21.32, 14.41) * mm});
            skArc(sketch, "E31.0.1", {"start": v(-21.32, 14.41) * mm, "mid": v(-21.12, 14.15) * mm, "end": v(-20.86, 13.93) * mm});
            skLineSegment(sketch, "E31.0.2", {"start": v(-20.86, 13.93) * mm, "end": v(-19.76, 13.2) * mm});
            skArc(sketch, "E31.0.3", {"start": v(-19.76, 13.2) * mm, "mid": v(-19.1, 12.24) * mm, "end": v(-19.26, 11.08) * mm});
            skArc(sketch, "E31.0.4", {"start": v(-19.26, 11.08) * mm, "mid": v(-19.6, 10.48) * mm, "end": v(-19.92, 9.86) * mm});
            skArc(sketch, "E31.0.5", {"start": v(-19.92, 9.86) * mm, "mid": v(-20.78, 9.08) * mm, "end": v(-21.95, 9.1) * mm});
            skLineSegment(sketch, "E31.0.6", {"start": v(-21.95, 9.1) * mm, "end": v(-23.17, 9.6) * mm});
            skArc(sketch, "E31.0.7", {"start": v(-23.17, 9.6) * mm, "mid": v(-23.5, 9.7) * mm, "end": v(-23.83, 9.72) * mm});
            skArc(sketch, "E31.0.8", {"start": v(-23.83, 9.72) * mm, "mid": v(-25.55, 9.43) * mm, "end": v(-27.12, 8.68) * mm});
            skArc(sketch, "E31.0.9", {"start": v(-27.12, 8.68) * mm, "mid": v(-27.23, 8.58) * mm, "end": v(-27.31, 8.45) * mm});
            skLineSegment(sketch, "E31.0.10", {"start": v(-27.31, 8.45) * mm, "end": v(-27.37, 8.3) * mm});
            skLineSegment(sketch, "E31.0.11", {"start": v(-27.37, 8.3) * mm, "end": v(-27.4, 8.15) * mm});
            skArc(sketch, "E31.0.12", {"start": v(-27.4, 8.15) * mm, "mid": v(-27.41, 8) * mm, "end": v(-27.37, 7.85) * mm});
            skArc(sketch, "E31.0.13", {"start": v(-27.37, 7.85) * mm, "mid": v(-26.48, 6.35) * mm, "end": v(-25.22, 5.15) * mm});
            skArc(sketch, "E31.0.14", {"start": v(-25.22, 5.15) * mm, "mid": v(-24.92, 4.99) * mm, "end": v(-24.6, 4.89) * mm});
            skLineSegment(sketch, "E31.0.15", {"start": v(-24.6, 4.89) * mm, "end": v(-23.3, 4.63) * mm});
            skArc(sketch, "E31.0.16", {"start": v(-23.3, 4.63) * mm, "mid": v(-22.32, 4) * mm, "end": v(-22.04, 2.87) * mm});
            skArc(sketch, "E31.0.17", {"start": v(-22.04, 2.87) * mm, "mid": v(-22.12, 2.18) * mm, "end": v(-22.18, 1.49) * mm});
            skArc(sketch, "E31.0.18", {"start": v(-22.18, 1.49) * mm, "mid": v(-22.67, 0.43) * mm, "end": v(-23.76, 0) * mm});
            skLineSegment(sketch, "E31.0.19", {"start": v(-23.76, 0) * mm, "end": v(-25.08, 0) * mm});
            skArc(sketch, "E31.0.20", {"start": v(-25.08, 0) * mm, "mid": v(-25.42, -0.03) * mm, "end": v(-25.74, -0.14) * mm});
            skArc(sketch, "E31.0.21", {"start": v(-25.74, -0.14) * mm, "mid": v(-27.21, -1.06) * mm, "end": v(-28.38, -2.36) * mm});
            skArc(sketch, "E31.0.22", {"start": v(-28.38, -2.36) * mm, "mid": v(-28.44, -2.5) * mm, "end": v(-28.47, -2.64) * mm});
            skLineSegment(sketch, "E31.0.23", {"start": v(-28.47, -2.64) * mm, "end": v(-28.47, -2.8) * mm});
            skLineSegment(sketch, "E31.0.24", {"start": v(-28.47, -2.8) * mm, "end": v(-28.44, -2.96) * mm});
            skArc(sketch, "E31.0.25", {"start": v(-28.44, -2.96) * mm, "mid": v(-28.38, -3.1) * mm, "end": v(-28.3, -3.22) * mm});
            skArc(sketch, "E31.0.26", {"start": v(-28.3, -3.22) * mm, "mid": v(-26.9, -4.27) * mm, "end": v(-25.27, -4.89) * mm});
            skArc(sketch, "E31.0.27", {"start": v(-25.27, -4.89) * mm, "mid": v(-24.94, -4.93) * mm, "end": v(-24.6, -4.9) * mm});
            skLineSegment(sketch, "E31.0.28", {"start": v(-24.6, -4.9) * mm, "end": v(-23.3, -4.64) * mm});
            skArc(sketch, "E31.0.29", {"start": v(-23.3, -4.64) * mm, "mid": v(-22.15, -4.85) * mm, "end": v(-21.46, -5.78) * mm});
            skArc(sketch, "E31.0.30", {"start": v(-21.46, -5.78) * mm, "mid": v(-21.27, -6.45) * mm, "end": v(-21.06, -7.11) * mm});
            skArc(sketch, "E31.0.31", {"start": v(-21.06, -7.11) * mm, "mid": v(-21.11, -8.28) * mm, "end": v(-21.95, -9.09) * mm});
            skLineSegment(sketch, "E31.0.32", {"start": v(-21.95, -9.09) * mm, "end": v(-23.18, -9.6) * mm});
            skArc(sketch, "E31.0.33", {"start": v(-23.18, -9.6) * mm, "mid": v(-23.47, -9.75) * mm, "end": v(-23.73, -9.97) * mm});
            skArc(sketch, "E31.0.34", {"start": v(-23.73, -9.97) * mm, "mid": v(-24.73, -11.4) * mm, "end": v(-25.32, -13.04) * mm});
            skArc(sketch, "E31.0.35", {"start": v(-25.32, -13.04) * mm, "mid": v(-25.32, -13.2) * mm, "end": v(-25.29, -13.34) * mm});
            skLineSegment(sketch, "E31.0.36", {"start": v(-25.29, -13.34) * mm, "end": v(-25.23, -13.48) * mm});
            skLineSegment(sketch, "E31.0.37", {"start": v(-25.23, -13.48) * mm, "end": v(-25.14, -13.62) * mm});
            skArc(sketch, "E31.0.38", {"start": v(-25.14, -13.62) * mm, "mid": v(-25.04, -13.73) * mm, "end": v(-24.9, -13.8) * mm});
            skArc(sketch, "E31.0.39", {"start": v(-24.9, -13.8) * mm, "mid": v(-23.22, -14.23) * mm, "end": v(-21.47, -14.19) * mm});
            skArc(sketch, "E31.0.40", {"start": v(-21.47, -14.19) * mm, "mid": v(-21.15, -14.1) * mm, "end": v(-20.85, -13.94) * mm});
            skLineSegment(sketch, "E31.0.41", {"start": v(-20.85, -13.94) * mm, "end": v(-19.75, -13.2) * mm});
            skArc(sketch, "E31.0.42", {"start": v(-19.75, -13.2) * mm, "mid": v(-18.61, -12.96) * mm, "end": v(-17.61, -13.56) * mm});
            skArc(sketch, "E31.0.43", {"start": v(-17.61, -13.56) * mm, "mid": v(-17.18, -14.1) * mm, "end": v(-16.73, -14.63) * mm});
            skArc(sketch, "E31.0.44", {"start": v(-16.73, -14.63) * mm, "mid": v(-16.34, -15.73) * mm, "end": v(-16.8, -16.8) * mm});
            skLineSegment(sketch, "E31.0.45", {"start": v(-16.8, -16.8) * mm, "end": v(-17.74, -17.73) * mm});
            skArc(sketch, "E31.0.46", {"start": v(-17.74, -17.73) * mm, "mid": v(-17.95, -18) * mm, "end": v(-18.1, -18.3) * mm});
            skArc(sketch, "E31.0.47", {"start": v(-18.1, -18.3) * mm, "mid": v(-18.49, -20) * mm, "end": v(-18.4, -21.74) * mm});
            skArc(sketch, "E31.0.48", {"start": v(-18.4, -21.74) * mm, "mid": v(-18.35, -21.88) * mm, "end": v(-18.26, -22) * mm});
            skLineSegment(sketch, "E31.0.49", {"start": v(-18.26, -22) * mm, "end": v(-18.15, -22.11) * mm});
            skLineSegment(sketch, "E31.0.50", {"start": v(-18.15, -22.11) * mm, "end": v(-18.01, -22.2) * mm});
            skArc(sketch, "E31.0.51", {"start": v(-18.01, -22.2) * mm, "mid": v(-17.88, -22.26) * mm, "end": v(-17.73, -22.29) * mm});
            skArc(sketch, "E31.0.52", {"start": v(-17.73, -22.29) * mm, "mid": v(-16, -22.03) * mm, "end": v(-14.41, -21.32) * mm});
            skArc(sketch, "E31.0.53", {"start": v(-14.41, -21.32) * mm, "mid": v(-14.15, -21.12) * mm, "end": v(-13.93, -20.86) * mm});
            skLineSegment(sketch, "E31.0.54", {"start": v(-13.93, -20.86) * mm, "end": v(-13.2, -19.76) * mm});
            skArc(sketch, "E31.0.55", {"start": v(-13.2, -19.76) * mm, "mid": v(-12.24, -19.1) * mm, "end": v(-11.08, -19.26) * mm});
            skArc(sketch, "E31.0.56", {"start": v(-11.08, -19.26) * mm, "mid": v(-10.48, -19.6) * mm, "end": v(-9.86, -19.92) * mm});
            skArc(sketch, "E31.0.57", {"start": v(-9.86, -19.92) * mm, "mid": v(-9.08, -20.78) * mm, "end": v(-9.1, -21.95) * mm});
            skLineSegment(sketch, "E31.0.58", {"start": v(-9.1, -21.95) * mm, "end": v(-9.6, -23.17) * mm});
            skArc(sketch, "E31.0.59", {"start": v(-9.6, -23.17) * mm, "mid": v(-9.7, -23.5) * mm, "end": v(-9.72, -23.83) * mm});
            skArc(sketch, "E31.0.60", {"start": v(-9.72, -23.83) * mm, "mid": v(-9.43, -25.55) * mm, "end": v(-8.68, -27.12) * mm});
            skArc(sketch, "E31.0.61", {"start": v(-8.68, -27.12) * mm, "mid": v(-8.58, -27.23) * mm, "end": v(-8.45, -27.31) * mm});
            skLineSegment(sketch, "E31.0.62", {"start": v(-8.45, -27.31) * mm, "end": v(-8.3, -27.37) * mm});
            skLineSegment(sketch, "E31.0.63", {"start": v(-8.3, -27.37) * mm, "end": v(-8.15, -27.4) * mm});
            skArc(sketch, "E31.0.64", {"start": v(-8.15, -27.4) * mm, "mid": v(-8, -27.41) * mm, "end": v(-7.85, -27.37) * mm});
            skArc(sketch, "E31.0.65", {"start": v(-7.85, -27.37) * mm, "mid": v(-6.35, -26.48) * mm, "end": v(-5.15, -25.22) * mm});
            skArc(sketch, "E31.0.66", {"start": v(-5.15, -25.22) * mm, "mid": v(-4.99, -24.92) * mm, "end": v(-4.89, -24.6) * mm});
            skLineSegment(sketch, "E31.0.67", {"start": v(-4.89, -24.6) * mm, "end": v(-4.63, -23.3) * mm});
            skArc(sketch, "E31.0.68", {"start": v(-4.63, -23.3) * mm, "mid": v(-4, -22.32) * mm, "end": v(-2.87, -22.04) * mm});
            skArc(sketch, "E31.0.69", {"start": v(-2.87, -22.04) * mm, "mid": v(-2.18, -22.12) * mm, "end": v(-1.49, -22.18) * mm});
            skArc(sketch, "E31.0.70", {"start": v(-1.49, -22.18) * mm, "mid": v(-0.43, -22.67) * mm, "end": v(0, -23.76) * mm});
            skLineSegment(sketch, "E31.0.71", {"start": v(0, -23.76) * mm, "end": v(0, -25.08) * mm});
            skArc(sketch, "E31.0.72", {"start": v(0, -25.08) * mm, "mid": v(0.03, -25.42) * mm, "end": v(0.14, -25.74) * mm});
            skArc(sketch, "E31.0.73", {"start": v(0.14, -25.74) * mm, "mid": v(1.06, -27.21) * mm, "end": v(2.36, -28.38) * mm});
            skArc(sketch, "E31.0.74", {"start": v(2.36, -28.38) * mm, "mid": v(2.5, -28.44) * mm, "end": v(2.64, -28.47) * mm});
            skLineSegment(sketch, "E31.0.75", {"start": v(2.64, -28.47) * mm, "end": v(2.8, -28.47) * mm});
            skLineSegment(sketch, "E31.0.76", {"start": v(2.8, -28.47) * mm, "end": v(2.96, -28.44) * mm});
            skArc(sketch, "E31.0.77", {"start": v(2.96, -28.44) * mm, "mid": v(3.1, -28.38) * mm, "end": v(3.22, -28.3) * mm});
            skArc(sketch, "E31.0.78", {"start": v(3.22, -28.3) * mm, "mid": v(4.27, -26.9) * mm, "end": v(4.89, -25.27) * mm});
            skArc(sketch, "E31.0.79", {"start": v(4.89, -25.27) * mm, "mid": v(4.93, -24.94) * mm, "end": v(4.9, -24.6) * mm});
            skLineSegment(sketch, "E31.0.80", {"start": v(4.9, -24.6) * mm, "end": v(4.64, -23.3) * mm});
            skArc(sketch, "E31.0.81", {"start": v(4.64, -23.3) * mm, "mid": v(4.85, -22.15) * mm, "end": v(5.78, -21.46) * mm});
            skArc(sketch, "E31.0.82", {"start": v(5.78, -21.46) * mm, "mid": v(6.45, -21.27) * mm, "end": v(7.11, -21.06) * mm});
            skArc(sketch, "E31.0.83", {"start": v(7.11, -21.06) * mm, "mid": v(8.28, -21.11) * mm, "end": v(9.09, -21.95) * mm});
            skLineSegment(sketch, "E31.0.84", {"start": v(9.09, -21.95) * mm, "end": v(9.6, -23.18) * mm});
            skArc(sketch, "E31.0.85", {"start": v(9.6, -23.18) * mm, "mid": v(9.75, -23.47) * mm, "end": v(9.97, -23.73) * mm});
            skArc(sketch, "E31.0.86", {"start": v(9.97, -23.73) * mm, "mid": v(11.4, -24.73) * mm, "end": v(13.04, -25.32) * mm});
            skArc(sketch, "E31.0.87", {"start": v(13.04, -25.32) * mm, "mid": v(13.2, -25.32) * mm, "end": v(13.34, -25.29) * mm});
            skLineSegment(sketch, "E31.0.88", {"start": v(13.34, -25.29) * mm, "end": v(13.48, -25.23) * mm});
            skLineSegment(sketch, "E31.0.89", {"start": v(13.48, -25.23) * mm, "end": v(13.62, -25.14) * mm});
            skArc(sketch, "E31.0.90", {"start": v(13.62, -25.14) * mm, "mid": v(13.73, -25.04) * mm, "end": v(13.8, -24.9) * mm});
            skArc(sketch, "E31.0.91", {"start": v(13.8, -24.9) * mm, "mid": v(14.23, -23.22) * mm, "end": v(14.19, -21.47) * mm});
            skArc(sketch, "E31.0.92", {"start": v(14.19, -21.47) * mm, "mid": v(14.1, -21.15) * mm, "end": v(13.94, -20.85) * mm});
            skLineSegment(sketch, "E31.0.93", {"start": v(13.94, -20.85) * mm, "end": v(13.2, -19.75) * mm});
            skArc(sketch, "E31.0.94", {"start": v(13.2, -19.75) * mm, "mid": v(12.96, -18.61) * mm, "end": v(13.56, -17.61) * mm});
            skArc(sketch, "E31.0.95", {"start": v(13.56, -17.61) * mm, "mid": v(14.1, -17.18) * mm, "end": v(14.63, -16.73) * mm});
            skArc(sketch, "E31.0.96", {"start": v(14.63, -16.73) * mm, "mid": v(15.73, -16.34) * mm, "end": v(16.8, -16.8) * mm});
            skLineSegment(sketch, "E31.0.97", {"start": v(16.8, -16.8) * mm, "end": v(17.73, -17.74) * mm});
            skArc(sketch, "E31.0.98", {"start": v(17.73, -17.74) * mm, "mid": v(18, -17.95) * mm, "end": v(18.3, -18.1) * mm});
            skArc(sketch, "E31.0.99", {"start": v(18.3, -18.1) * mm, "mid": v(20, -18.49) * mm, "end": v(21.74, -18.4) * mm});
            skArc(sketch, "E31.0.100", {"start": v(21.74, -18.4) * mm, "mid": v(21.88, -18.35) * mm, "end": v(22, -18.26) * mm});
            skLineSegment(sketch, "E31.0.101", {"start": v(22, -18.26) * mm, "end": v(22.11, -18.15) * mm});
            skLineSegment(sketch, "E31.0.102", {"start": v(22.11, -18.15) * mm, "end": v(22.2, -18.01) * mm});
            skArc(sketch, "E31.0.103", {"start": v(22.2, -18.01) * mm, "mid": v(22.26, -17.88) * mm, "end": v(22.29, -17.73) * mm});
            skArc(sketch, "E31.0.104", {"start": v(22.29, -17.73) * mm, "mid": v(22.03, -16) * mm, "end": v(21.32, -14.41) * mm});
            skArc(sketch, "E31.0.105", {"start": v(21.32, -14.41) * mm, "mid": v(21.12, -14.15) * mm, "end": v(20.86, -13.93) * mm});
            skLineSegment(sketch, "E31.0.106", {"start": v(20.86, -13.93) * mm, "end": v(19.76, -13.2) * mm});
            skArc(sketch, "E31.0.107", {"start": v(19.76, -13.2) * mm, "mid": v(19.1, -12.24) * mm, "end": v(19.26, -11.08) * mm});
            skArc(sketch, "E31.0.108", {"start": v(19.26, -11.08) * mm, "mid": v(19.6, -10.48) * mm, "end": v(19.92, -9.86) * mm});
            skArc(sketch, "E31.0.109", {"start": v(19.92, -9.86) * mm, "mid": v(20.78, -9.08) * mm, "end": v(21.95, -9.1) * mm});
            skLineSegment(sketch, "E31.0.110", {"start": v(21.95, -9.1) * mm, "end": v(23.17, -9.6) * mm});
            skArc(sketch, "E31.0.111", {"start": v(23.17, -9.6) * mm, "mid": v(23.5, -9.7) * mm, "end": v(23.83, -9.72) * mm});
            skArc(sketch, "E31.0.112", {"start": v(23.83, -9.72) * mm, "mid": v(25.55, -9.43) * mm, "end": v(27.12, -8.68) * mm});
            skArc(sketch, "E31.0.113", {"start": v(27.12, -8.68) * mm, "mid": v(27.23, -8.58) * mm, "end": v(27.31, -8.45) * mm});
            skLineSegment(sketch, "E31.0.114", {"start": v(27.31, -8.45) * mm, "end": v(27.37, -8.3) * mm});
            skLineSegment(sketch, "E31.0.115", {"start": v(27.37, -8.3) * mm, "end": v(27.4, -8.15) * mm});
            skArc(sketch, "E31.0.116", {"start": v(27.4, -8.15) * mm, "mid": v(27.41, -8) * mm, "end": v(27.37, -7.85) * mm});
            skArc(sketch, "E31.0.117", {"start": v(27.37, -7.85) * mm, "mid": v(26.48, -6.35) * mm, "end": v(25.22, -5.15) * mm});
            skArc(sketch, "E31.0.118", {"start": v(25.22, -5.15) * mm, "mid": v(24.92, -4.99) * mm, "end": v(24.6, -4.89) * mm});
            skLineSegment(sketch, "E31.0.119", {"start": v(24.6, -4.89) * mm, "end": v(23.3, -4.63) * mm});
            skArc(sketch, "E31.0.120", {"start": v(23.3, -4.63) * mm, "mid": v(22.32, -4) * mm, "end": v(22.04, -2.87) * mm});
            skArc(sketch, "E31.0.121", {"start": v(22.04, -2.87) * mm, "mid": v(22.12, -2.18) * mm, "end": v(22.18, -1.49) * mm});
            skArc(sketch, "E31.0.122", {"start": v(22.18, -1.49) * mm, "mid": v(22.67, -0.43) * mm, "end": v(23.76, 0) * mm});
            skLineSegment(sketch, "E31.0.123", {"start": v(23.76, 0) * mm, "end": v(25.08, 0) * mm});
            skArc(sketch, "E31.0.124", {"start": v(25.08, 0) * mm, "mid": v(25.42, 0.03) * mm, "end": v(25.74, 0.14) * mm});
            skArc(sketch, "E31.0.125", {"start": v(25.74, 0.14) * mm, "mid": v(27.21, 1.06) * mm, "end": v(28.38, 2.36) * mm});
            skArc(sketch, "E31.0.126", {"start": v(28.38, 2.36) * mm, "mid": v(28.44, 2.5) * mm, "end": v(28.47, 2.64) * mm});
            skLineSegment(sketch, "E31.0.127", {"start": v(28.47, 2.64) * mm, "end": v(28.47, 2.8) * mm});
            skLineSegment(sketch, "E31.0.128", {"start": v(28.47, 2.8) * mm, "end": v(28.44, 2.96) * mm});
            skArc(sketch, "E31.0.129", {"start": v(28.44, 2.96) * mm, "mid": v(28.38, 3.1) * mm, "end": v(28.3, 3.22) * mm});
            skArc(sketch, "E31.0.130", {"start": v(28.3, 3.22) * mm, "mid": v(26.9, 4.27) * mm, "end": v(25.27, 4.89) * mm});
            skArc(sketch, "E31.0.131", {"start": v(25.27, 4.89) * mm, "mid": v(24.94, 4.93) * mm, "end": v(24.6, 4.9) * mm});
            skLineSegment(sketch, "E31.0.132", {"start": v(24.6, 4.9) * mm, "end": v(23.3, 4.64) * mm});
            skArc(sketch, "E31.0.133", {"start": v(23.3, 4.64) * mm, "mid": v(22.15, 4.85) * mm, "end": v(21.46, 5.78) * mm});
            skArc(sketch, "E31.0.134", {"start": v(21.46, 5.78) * mm, "mid": v(21.27, 6.45) * mm, "end": v(21.06, 7.11) * mm});
            skArc(sketch, "E31.0.135", {"start": v(21.06, 7.11) * mm, "mid": v(21.11, 8.28) * mm, "end": v(21.95, 9.09) * mm});
            skLineSegment(sketch, "E31.0.136", {"start": v(21.95, 9.09) * mm, "end": v(23.18, 9.6) * mm});
            skArc(sketch, "E31.0.137", {"start": v(23.18, 9.6) * mm, "mid": v(23.47, 9.75) * mm, "end": v(23.73, 9.97) * mm});
            skArc(sketch, "E31.0.138", {"start": v(23.73, 9.97) * mm, "mid": v(24.73, 11.4) * mm, "end": v(25.32, 13.04) * mm});
            skArc(sketch, "E31.0.139", {"start": v(25.32, 13.04) * mm, "mid": v(25.32, 13.2) * mm, "end": v(25.29, 13.34) * mm});
            skLineSegment(sketch, "E31.0.140", {"start": v(25.29, 13.34) * mm, "end": v(25.23, 13.48) * mm});
            skLineSegment(sketch, "E31.0.141", {"start": v(25.23, 13.48) * mm, "end": v(25.14, 13.62) * mm});
            skArc(sketch, "E31.0.142", {"start": v(25.14, 13.62) * mm, "mid": v(25.04, 13.73) * mm, "end": v(24.9, 13.8) * mm});
            skArc(sketch, "E31.0.143", {"start": v(24.9, 13.8) * mm, "mid": v(23.22, 14.23) * mm, "end": v(21.47, 14.19) * mm});
            skArc(sketch, "E31.0.144", {"start": v(21.47, 14.19) * mm, "mid": v(21.15, 14.1) * mm, "end": v(20.85, 13.94) * mm});
            skLineSegment(sketch, "E31.0.145", {"start": v(20.85, 13.94) * mm, "end": v(19.75, 13.2) * mm});
            skArc(sketch, "E31.0.146", {"start": v(19.75, 13.2) * mm, "mid": v(18.61, 12.96) * mm, "end": v(17.61, 13.56) * mm});
            skArc(sketch, "E31.0.147", {"start": v(17.61, 13.56) * mm, "mid": v(17.18, 14.1) * mm, "end": v(16.73, 14.63) * mm});
            skArc(sketch, "E31.0.148", {"start": v(16.73, 14.63) * mm, "mid": v(16.34, 15.73) * mm, "end": v(16.8, 16.8) * mm});
            skLineSegment(sketch, "E31.0.149", {"start": v(16.8, 16.8) * mm, "end": v(17.74, 17.73) * mm});
            skArc(sketch, "E31.0.150", {"start": v(17.74, 17.73) * mm, "mid": v(17.95, 18) * mm, "end": v(18.1, 18.3) * mm});
            skArc(sketch, "E31.0.151", {"start": v(18.1, 18.3) * mm, "mid": v(18.49, 20) * mm, "end": v(18.4, 21.74) * mm});
            skArc(sketch, "E31.0.152", {"start": v(18.4, 21.74) * mm, "mid": v(18.35, 21.88) * mm, "end": v(18.26, 22) * mm});
            skLineSegment(sketch, "E31.0.153", {"start": v(18.26, 22) * mm, "end": v(18.15, 22.11) * mm});
            skLineSegment(sketch, "E31.0.154", {"start": v(18.15, 22.11) * mm, "end": v(18.01, 22.2) * mm});
            skArc(sketch, "E31.0.155", {"start": v(18.01, 22.2) * mm, "mid": v(17.88, 22.26) * mm, "end": v(17.73, 22.29) * mm});
            skArc(sketch, "E31.0.156", {"start": v(17.73, 22.29) * mm, "mid": v(16, 22.03) * mm, "end": v(14.41, 21.32) * mm});
            skArc(sketch, "E31.0.157", {"start": v(14.41, 21.32) * mm, "mid": v(14.15, 21.12) * mm, "end": v(13.93, 20.86) * mm});
            skLineSegment(sketch, "E31.0.158", {"start": v(13.93, 20.86) * mm, "end": v(13.2, 19.76) * mm});
            skArc(sketch, "E31.0.159", {"start": v(13.2, 19.76) * mm, "mid": v(12.24, 19.1) * mm, "end": v(11.08, 19.26) * mm});
            skArc(sketch, "E31.0.160", {"start": v(11.08, 19.26) * mm, "mid": v(10.48, 19.6) * mm, "end": v(9.86, 19.92) * mm});
            skArc(sketch, "E31.0.161", {"start": v(9.86, 19.92) * mm, "mid": v(9.08, 20.78) * mm, "end": v(9.1, 21.95) * mm});
            skLineSegment(sketch, "E31.0.162", {"start": v(9.1, 21.95) * mm, "end": v(9.6, 23.17) * mm});
            skArc(sketch, "E31.0.163", {"start": v(9.6, 23.17) * mm, "mid": v(9.7, 23.5) * mm, "end": v(9.72, 23.83) * mm});
            skArc(sketch, "E31.0.164", {"start": v(9.72, 23.83) * mm, "mid": v(9.43, 25.55) * mm, "end": v(8.68, 27.12) * mm});
            skArc(sketch, "E31.0.165", {"start": v(8.68, 27.12) * mm, "mid": v(8.58, 27.23) * mm, "end": v(8.45, 27.31) * mm});
            skLineSegment(sketch, "E31.0.166", {"start": v(8.45, 27.31) * mm, "end": v(8.3, 27.37) * mm});
            skLineSegment(sketch, "E31.0.167", {"start": v(8.3, 27.37) * mm, "end": v(8.15, 27.4) * mm});
            skArc(sketch, "E31.0.168", {"start": v(8.15, 27.4) * mm, "mid": v(8, 27.41) * mm, "end": v(7.85, 27.37) * mm});
            skArc(sketch, "E31.0.169", {"start": v(7.85, 27.37) * mm, "mid": v(6.35, 26.48) * mm, "end": v(5.15, 25.22) * mm});
            skArc(sketch, "E31.0.170", {"start": v(5.15, 25.22) * mm, "mid": v(4.99, 24.92) * mm, "end": v(4.89, 24.6) * mm});
            skLineSegment(sketch, "E31.0.171", {"start": v(4.89, 24.6) * mm, "end": v(4.63, 23.3) * mm});
            skArc(sketch, "E31.0.172", {"start": v(4.63, 23.3) * mm, "mid": v(4, 22.32) * mm, "end": v(2.87, 22.04) * mm});
            skArc(sketch, "E31.0.173", {"start": v(2.87, 22.04) * mm, "mid": v(2.18, 22.12) * mm, "end": v(1.49, 22.18) * mm});
            skArc(sketch, "E31.0.174", {"start": v(1.49, 22.18) * mm, "mid": v(0.43, 22.67) * mm, "end": v(0, 23.76) * mm});
            skLineSegment(sketch, "E31.0.175", {"start": v(0, 23.76) * mm, "end": v(0, 25.08) * mm});
            skArc(sketch, "E31.0.176", {"start": v(0, 25.08) * mm, "mid": v(-0.03, 25.42) * mm, "end": v(-0.14, 25.74) * mm});
            skArc(sketch, "E31.0.177", {"start": v(-0.14, 25.74) * mm, "mid": v(-1.06, 27.21) * mm, "end": v(-2.36, 28.38) * mm});
            skArc(sketch, "E31.0.178", {"start": v(-2.36, 28.38) * mm, "mid": v(-2.5, 28.44) * mm, "end": v(-2.64, 28.47) * mm});
            skLineSegment(sketch, "E31.0.179", {"start": v(-2.64, 28.47) * mm, "end": v(-2.8, 28.47) * mm});
            skLineSegment(sketch, "E31.0.180", {"start": v(-2.8, 28.47) * mm, "end": v(-2.96, 28.44) * mm});
            skArc(sketch, "E31.0.181", {"start": v(-2.96, 28.44) * mm, "mid": v(-3.1, 28.38) * mm, "end": v(-3.22, 28.3) * mm});
            skArc(sketch, "E31.0.182", {"start": v(-3.22, 28.3) * mm, "mid": v(-4.27, 26.9) * mm, "end": v(-4.89, 25.27) * mm});
            skArc(sketch, "E31.0.183", {"start": v(-4.89, 25.27) * mm, "mid": v(-4.93, 24.94) * mm, "end": v(-4.9, 24.6) * mm});
            skLineSegment(sketch, "E31.0.184", {"start": v(-4.9, 24.6) * mm, "end": v(-4.64, 23.3) * mm});
            skArc(sketch, "E31.0.185", {"start": v(-4.64, 23.3) * mm, "mid": v(-4.85, 22.15) * mm, "end": v(-5.78, 21.46) * mm});
            skArc(sketch, "E31.0.186", {"start": v(-5.78, 21.46) * mm, "mid": v(-6.45, 21.27) * mm, "end": v(-7.11, 21.06) * mm});
            skArc(sketch, "E31.0.187", {"start": v(-7.11, 21.06) * mm, "mid": v(-8.28, 21.11) * mm, "end": v(-9.09, 21.95) * mm});
            skLineSegment(sketch, "E31.0.188", {"start": v(-9.09, 21.95) * mm, "end": v(-9.6, 23.18) * mm});
            skArc(sketch, "E31.0.189", {"start": v(-9.6, 23.18) * mm, "mid": v(-9.75, 23.47) * mm, "end": v(-9.97, 23.73) * mm});
            skArc(sketch, "E31.0.190", {"start": v(-9.97, 23.73) * mm, "mid": v(-11.4, 24.73) * mm, "end": v(-13.04, 25.32) * mm});
            skArc(sketch, "E31.0.191", {"start": v(-13.04, 25.32) * mm, "mid": v(-13.2, 25.32) * mm, "end": v(-13.34, 25.29) * mm});
            skLineSegment(sketch, "E31.0.192", {"start": v(-13.34, 25.29) * mm, "end": v(-13.48, 25.23) * mm});
            skLineSegment(sketch, "E31.0.193", {"start": v(-13.48, 25.23) * mm, "end": v(-13.62, 25.14) * mm});
            skArc(sketch, "E31.0.194", {"start": v(-13.62, 25.14) * mm, "mid": v(-13.73, 25.04) * mm, "end": v(-13.8, 24.9) * mm});
            skArc(sketch, "E31.0.195", {"start": v(-13.8, 24.9) * mm, "mid": v(-14.23, 23.22) * mm, "end": v(-14.19, 21.47) * mm});
            skArc(sketch, "E31.0.196", {"start": v(-14.19, 21.47) * mm, "mid": v(-14.1, 21.15) * mm, "end": v(-13.94, 20.85) * mm});
            skLineSegment(sketch, "E31.0.197", {"start": v(-13.94, 20.85) * mm, "end": v(-13.2, 19.75) * mm});
            skArc(sketch, "E31.0.198", {"start": v(-13.2, 19.75) * mm, "mid": v(-12.96, 18.61) * mm, "end": v(-13.56, 17.61) * mm});
            skArc(sketch, "E31.0.199", {"start": v(-13.56, 17.61) * mm, "mid": v(-14.1, 17.18) * mm, "end": v(-14.63, 16.73) * mm});
            skArc(sketch, "E31.0.200", {"start": v(-14.63, 16.73) * mm, "mid": v(-15.73, 16.34) * mm, "end": v(-16.8, 16.8) * mm});
            skLineSegment(sketch, "E31.0.201", {"start": v(-16.8, 16.8) * mm, "end": v(-17.73, 17.74) * mm});
            skArc(sketch, "E31.0.202", {"start": v(-17.73, 17.74) * mm, "mid": v(-18, 17.95) * mm, "end": v(-18.3, 18.1) * mm});
            skArc(sketch, "E31.0.203", {"start": v(-18.3, 18.1) * mm, "mid": v(-20, 18.49) * mm, "end": v(-21.74, 18.4) * mm});
            skArc(sketch, "E31.0.204", {"start": v(-21.74, 18.4) * mm, "mid": v(-21.88, 18.35) * mm, "end": v(-22, 18.26) * mm});
            skLineSegment(sketch, "E31.0.205", {"start": v(-22, 18.26) * mm, "end": v(-22.11, 18.15) * mm});
            skLineSegment(sketch, "E31.0.206", {"start": v(-22.11, 18.15) * mm, "end": v(-22.2, 18.01) * mm});
            skArc(sketch, "E31.0.207", {"start": v(-22.2, 18.01) * mm, "mid": v(-22.26, 17.88) * mm, "end": v(-22.29, 17.73) * mm});
            skSolve(sketch);
        }
        {
            var Q0;
            Q0=makeQuery(id+"F0.imprint","IMPRINT",FACE,{"disambiguationData":[TD([[makeQuery(id+"F0.imprint","IMPRINT",EDGE,{"derivedFrom":sQuery(id+"F0.wireOp",EDGE,"E0")}),1.0]])]});
            var Q1;
            Q1=makeQuery(id+"F2.imprint","IMPRINT",FACE,{"disambiguationData":[TD([[makeQuery(id+"F2.imprint","IMPRINT",EDGE,{"derivedFrom":sQuery(id+"F2.wireOp",EDGE,"E31.0.0")}),1.0]])]});
            var Q2;
            Q2=sQuery(id+"F2.wireOp",VERTEX,"E31.0.176.start");
            var Q3;
            Q3=sQuery(id+"F0.wireOp",VERTEX,"E15.1.9.start");
            loft(context, id + "F3", {"sheetProfilesArray" : [{ "sheetProfileEntities" : qUnion([Q0]) }, { "sheetProfileEntities" : qUnion([Q1]) }], "matchConnections" : true, "connections" : [{ "connectionEntities" : qUnion([Q2, Q3]), "connectionEdgeQueries" : qUnion([]), "connectionEdgeParameters" : [] }]});
        }
        {
            var Q0;
            Q0=makeQuery(id+"F3.opLoft","CAP_FACE",FACE,{"disambiguationData":[OSD([makeQuery(id+"F2.imprint","IMPRINT",FACE,{"disambiguationData":[TD([[makeQuery(id+"F2.imprint","IMPRINT",EDGE,{"derivedFrom":sQuery(id+"F2.wireOp",EDGE,"E31.0.0")}),1.0]])]})])],"isStart":true});
            var sketch = newSketch(context, id + "F4", { "sketchPlane" : qUnion([Q0])});
            skPoint(sketch, "E32", {"position": v(0, 0) * mm});
            skSolve(sketch);
        }
        {
            var Q0;
            Q0=sQuery(id+"F4.wireOp",VERTEX,"E32");
            var Q1;
            Q1=makeQuery(id+"F3.opLoft","SWEPT_BODY",BODY,{"disambiguationData":[OSD([makeQuery(id+"F0.imprint","IMPRINT",FACE,{"disambiguationData":[TD([[makeQuery(id+"F0.imprint","IMPRINT",EDGE,{"derivedFrom":sQuery(id+"F0.wireOp",EDGE,"E0")}),1.0]])]}),makeQuery(id+"F2.imprint","IMPRINT",FACE,{"disambiguationData":[TD([[makeQuery(id+"F2.imprint","IMPRINT",EDGE,{"derivedFrom":sQuery(id+"F2.wireOp",EDGE,"E31.0.0")}),1.0]])]})])]});
            hole(context, id + "F5", {"style" : HoleStyle.SIMPLE, "endStyle" : HoleEndStyle.THROUGH, "holeDiameter" : 12.7 * mm, "tappedDepth" : 12.7 * mm, "tapClearance" : 3, "locations" : qUnion([Q0]), "scope" : qUnion([Q1])});
        }
    });
